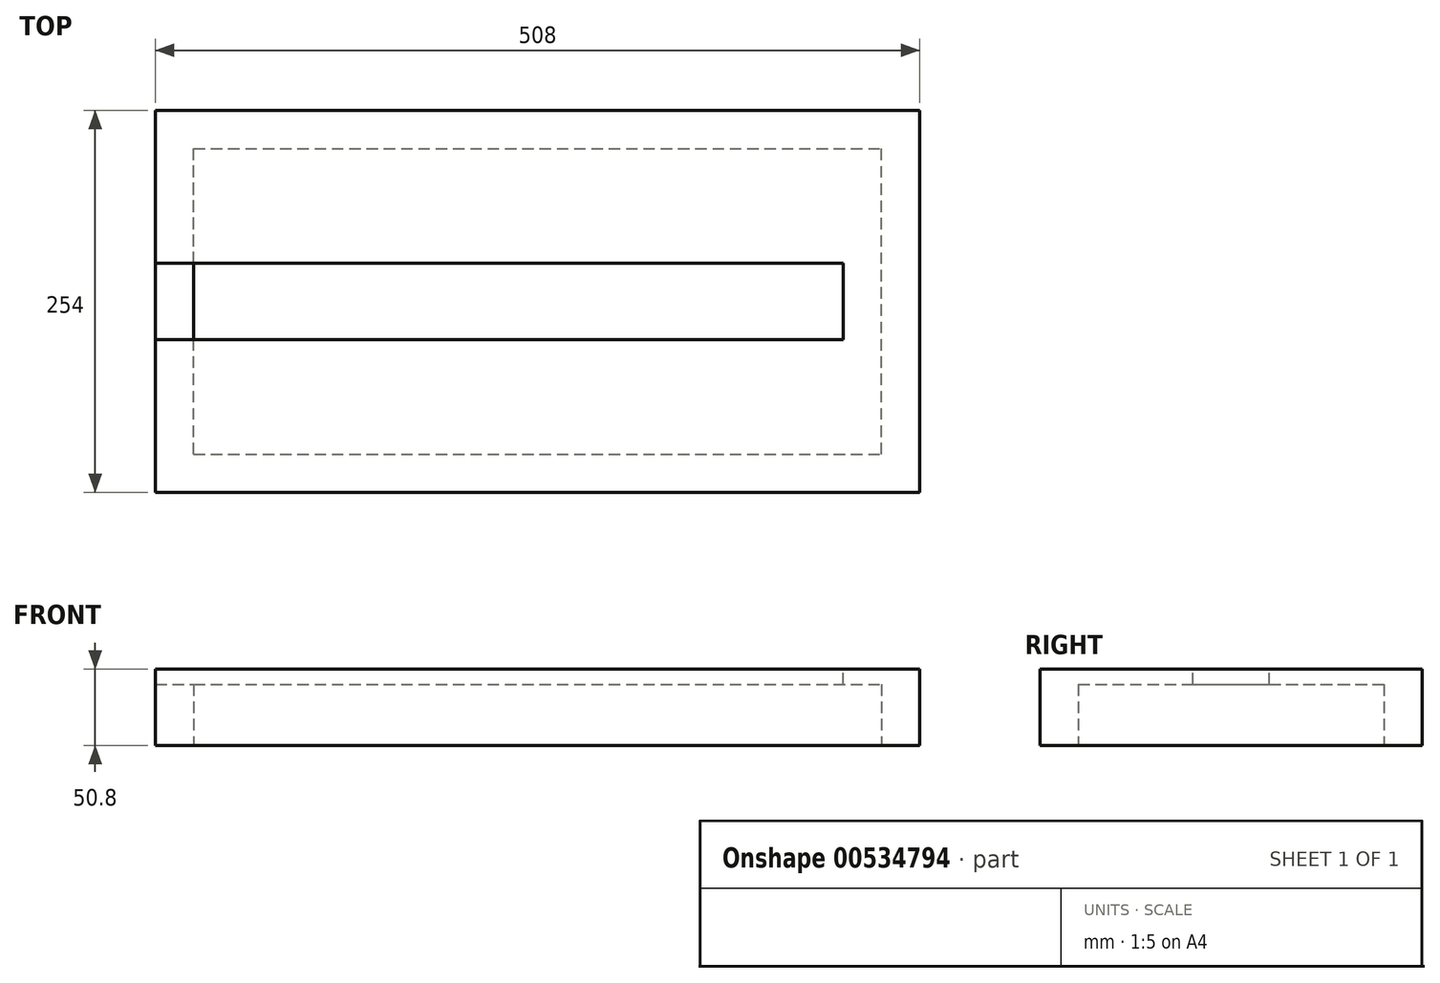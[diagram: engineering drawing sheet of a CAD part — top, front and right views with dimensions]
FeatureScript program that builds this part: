
annotation { "Feature Type Name" : "Feature", "Feature Type Description" : "" }
export const myFeature = defineFeature(function(context is Context, id is Id, definition is map)
    precondition{}
    {
        {
            var Q0;
            Q0=qCreatedBy(makeId("Top.planeOp"),FACE);
            var sketch = newSketch(context, id + "F0", { "sketchPlane" : qUnion([Q0])});
            skLineSegment(sketch, "E0.bottom", {"start": v(254, -127) * mm, "end": v(-254, -127) * mm});
            skLineSegment(sketch, "E0.top", {"start": v(254, 127) * mm, "end": v(-254, 127) * mm});
            skLineSegment(sketch, "E0.left", {"start": v(254, -127) * mm, "end": v(254, 127) * mm});
            skLineSegment(sketch, "E0.right", {"start": v(-254, -127) * mm, "end": v(-254, 127) * mm});
            skPoint(sketch, "E0.middle", {"position": v(0, 0) * mm});
            skSolve(sketch);
        }
        {
            var Q0;
            Q0 = qSketchRegion(id + "F0", true);
            extrude(context, id + "F1", {"entities" : qUnion([Q0]), "oppositeDirection" : true, "depth" : 50.8 * mm, "offsetDistance" : 25.4 * mm});
        }
        {
            var Q0;
            Q0=makeQuery(id+"F1.opExtrude","CAP_FACE",FACE,{"disambiguationData":[OSD([sQuery(id+"F0.wireOp",EDGE,"E0.bottom"),sQuery(id+"F0.wireOp",EDGE,"E0.top"),sQuery(id+"F0.wireOp",EDGE,"E0.left"),sQuery(id+"F0.wireOp",EDGE,"E0.right")])],"isStart":false});
            var sketch = newSketch(context, id + "F2", { "sketchPlane" : qUnion([Q0])});
            skLineSegment(sketch, "E1.bottom", {"start": v(-228.6, 101.6) * mm, "end": v(228.6, 101.6) * mm});
            skLineSegment(sketch, "E1.top", {"start": v(-228.6, -101.6) * mm, "end": v(228.6, -101.6) * mm});
            skLineSegment(sketch, "E1.left", {"start": v(-228.6, 101.6) * mm, "end": v(-228.6, -101.6) * mm});
            skLineSegment(sketch, "E1.right", {"start": v(228.6, 101.6) * mm, "end": v(228.6, -101.6) * mm});
            skPoint(sketch, "E1.middle", {"position": v(0, 0) * mm});
            skSolve(sketch);
        }
        {
            var Q0;
            Q0 = qSketchRegion(id + "F2", true);
            extrude(context, id + "F3", {"entities" : qUnion([Q0]), "operationType" : NewBodyOperationType.REMOVE, "oppositeDirection" : true, "depth" : 40.64 * mm, "offsetDistance" : 25.4 * mm});
        }
        {
            var Q0;
            Q0=makeQuery(id+"F1.opExtrude","CAP_FACE",FACE,{"disambiguationData":[OSD([sQuery(id+"F0.wireOp",EDGE,"E0.bottom"),sQuery(id+"F0.wireOp",EDGE,"E0.top"),sQuery(id+"F0.wireOp",EDGE,"E0.left"),sQuery(id+"F0.wireOp",EDGE,"E0.right")])],"isStart":true});
            var sketch = newSketch(context, id + "F4", { "sketchPlane" : qUnion([Q0])});
            skLineSegment(sketch, "E2.bottom", {"start": v(-254, 25.4) * mm, "end": v(203.2, 25.4) * mm});
            skLineSegment(sketch, "E2.top", {"start": v(-254, -25.4) * mm, "end": v(203.2, -25.4) * mm});
            skLineSegment(sketch, "E2.left", {"start": v(-254, 25.4) * mm, "end": v(-254, -25.4) * mm});
            skLineSegment(sketch, "E2.right", {"start": v(203.2, 25.4) * mm, "end": v(203.2, -25.4) * mm});
            skSolve(sketch);
        }
        {
            var Q0;
            Q0 = qSketchRegion(id + "F4", true);
            extrude(context, id + "F5", {"entities" : qUnion([Q0]), "operationType" : NewBodyOperationType.REMOVE, "oppositeDirection" : true, "depth" : 10.16 * mm, "offsetDistance" : 25.4 * mm});
        }
    });
